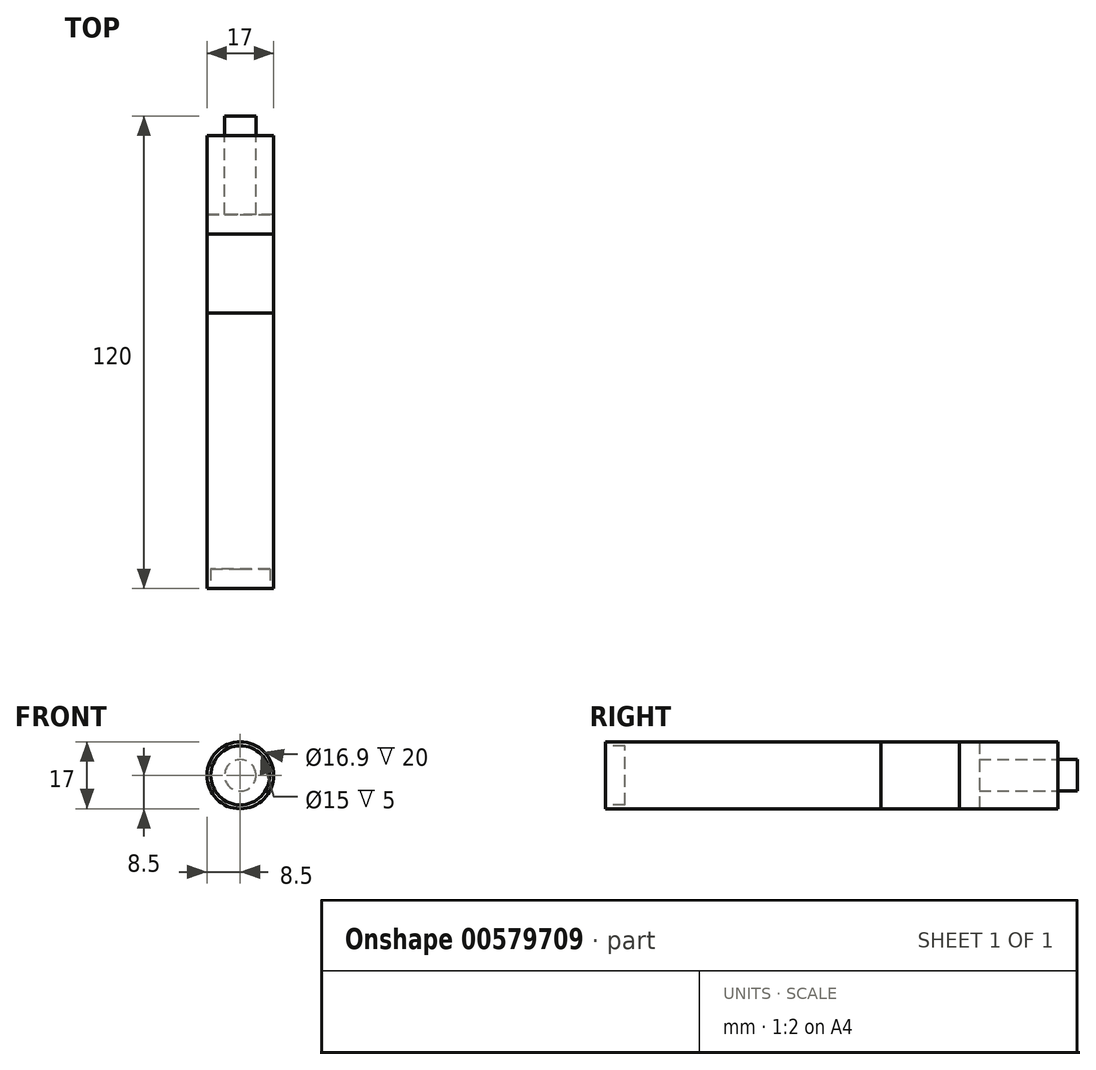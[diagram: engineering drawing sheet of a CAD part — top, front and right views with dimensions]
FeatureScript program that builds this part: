
annotation { "Feature Type Name" : "Feature", "Feature Type Description" : "" }
export const myFeature = defineFeature(function(context is Context, id is Id, definition is map)
    precondition{}
    {
        {
            var Q0;
            Q0=qCreatedBy(makeId("Front.planeOp"),FACE);
            var sketch = newSketch(context, id + "F0", { "sketchPlane" : qUnion([Q0])});
            skCircle(sketch, "E0", {"center": v(0, 0) * mm, "radius": 8.5 * mm});
            skSolve(sketch);
        }
        {
            var Q0;
            Q0=makeQuery(id+"F0.imprint","IMPRINT",FACE,{"disambiguationData":[TD([[makeQuery(id+"F0.imprint","IMPRINT",EDGE,{"derivedFrom":sQuery(id+"F0.wireOp",EDGE,"E0")}),1.0]])]});
            extrude(context, id + "F1", {"entities" : qUnion([Q0]), "depth" : 90 * mm, "offsetDistance" : 25 * mm});
        }
        {
            var Q0;
            Q0=qCreatedBy(makeId("Front.planeOp"),FACE);
            var sketch = newSketch(context, id + "F2", { "sketchPlane" : qUnion([Q0])});
            skCircle(sketch, "E1", {"center": v(0, 0) * mm, "radius": 8.5 * mm});
            skSolve(sketch);
        }
        {
            var Q0;
            Q0 = qSketchRegion(id + "F2", true);
            extrude(context, id + "F3", {"entities" : qUnion([Q0]), "depth" : 20 * mm, "offsetDistance" : 25 * mm, "hasSecondDirection" : true, "secondDirectionOppositeDirection" : true, "secondDirectionDepth" : 25 * mm});
        }
        {
            var Q0;
            Q0=makeQuery(id+"F3.opExtrude","CAP_FACE",FACE,{"disambiguationData":[OSD([sQuery(id+"F2.wireOp",EDGE,"E1")])],"isStart":true});
            var sketch = newSketch(context, id + "F4", { "sketchPlane" : qUnion([Q0])});
            skCircle(sketch, "E2", {"center": v(0, 0) * mm, "radius": 4 * mm});
            skSolve(sketch);
        }
        {
            var Q0;
            Q0 = qSketchRegion(id + "F4", true);
            extrude(context, id + "F5", {"entities" : qUnion([Q0]), "depth" : 5 * mm, "offsetDistance" : 25 * mm});
        }
        {
            var Q0;
            Q0=makeQuery(id+"F3.opExtrude","CAP_FACE",FACE,{"disambiguationData":[OSD([sQuery(id+"F2.wireOp",EDGE,"E1")])],"isStart":true});
            var sketch = newSketch(context, id + "F6", { "sketchPlane" : qUnion([Q0])});
            skCircle(sketch, "E3", {"center": v(0, 0) * mm, "radius": 8.45 * mm});
            skSolve(sketch);
        }
        {
            var Q0;
            Q0=makeQuery(id+"F6.imprint","IMPRINT",FACE,{"disambiguationData":[TD([[makeQuery(id+"F6.imprint","IMPRINT",EDGE,{"derivedFrom":sQuery(id+"F6.wireOp",EDGE,"E3")}),1.0]])]});
            extrude(context, id + "F7", {"entities" : qUnion([Q0]), "operationType" : NewBodyOperationType.REMOVE, "oppositeDirection" : true, "depth" : 20 * mm, "offsetDistance" : 25 * mm});
        }
        {
            var Q0;
            Q0 = qSketchRegion(id + "F4", true);
            extrude(context, id + "F8", {"entities" : qUnion([Q0]), "oppositeDirection" : true, "depth" : 20 * mm, "offsetDistance" : 25 * mm});
        }
        {
            var Q0;
            Q0=makeQuery(id+"F1.opExtrude","CAP_FACE",FACE,{"disambiguationData":[OSD([sQuery(id+"F0.wireOp",EDGE,"E0")])],"isStart":false});
            var sketch = newSketch(context, id + "F9", { "sketchPlane" : qUnion([Q0])});
            skCircle(sketch, "E4", {"center": v(0, 0) * mm, "radius": 8.5 * mm});
            skSolve(sketch);
        }
        {
            var Q0;
            Q0=makeQuery(id+"F9.imprint","IMPRINT",FACE,{"disambiguationData":[TD([[makeQuery(id+"F9.imprint","IMPRINT",EDGE,{"derivedFrom":sQuery(id+"F9.wireOp",EDGE,"E4")}),1.0]])]});
            var sketch = newSketch(context, id + "F10", { "sketchPlane" : qUnion([Q0])});
            skCircle(sketch, "E5", {"center": v(0, 0) * mm, "radius": 7.5 * mm});
            skSolve(sketch);
        }
        {
            var Q0;
            Q0 = qSketchRegion(id + "F10", true);
            extrude(context, id + "F11", {"entities" : qUnion([Q0]), "operationType" : NewBodyOperationType.REMOVE, "oppositeDirection" : true, "depth" : 5 * mm, "offsetDistance" : 25 * mm});
        }
        {
            var Q0;
            Q0=makeQuery(id+"F9.imprint","IMPRINT",FACE,{"disambiguationData":[TD([[makeQuery(id+"F9.imprint","IMPRINT",EDGE,{"derivedFrom":sQuery(id+"F9.wireOp",EDGE,"E4")}),1.0]])]});
            var sketch = newSketch(context, id + "F12", { "sketchPlane" : qUnion([Q0])});
            skLineSegment(sketch, "E6", {"start": v(0, -7.42) * mm, "end": v(0, -4.42) * mm});
            skLineSegment(sketch, "E7", {"start": v(0, 7.48) * mm, "end": v(0, 4.48) * mm});
            skLineSegment(sketch, "E8", {"start": v(-7.53, 0) * mm, "end": v(-4.53, 0) * mm});
            skLineSegment(sketch, "E9", {"start": v(7.45, 0) * mm, "end": v(4.45, 0) * mm});
            skSolve(sketch);
        }
        {
            var Q0;
            Q0=sQuery(id+"F12.wireOp",EDGE,"E7");
            extrude(context, id + "F13", {"bodyType" : ToolBodyType.SURFACE, "surfaceEntities" : qUnion([Q0]), "oppositeDirection" : true, "depth" : 5 * mm, "offsetDistance" : 25 * mm});
        }
        {
            var Q0;
            Q0=sQuery(id+"F12.wireOp",EDGE,"E8");
            extrude(context, id + "F14", {"bodyType" : ToolBodyType.SURFACE, "surfaceEntities" : qUnion([Q0]), "oppositeDirection" : true, "depth" : 5 * mm, "offsetDistance" : 25 * mm});
        }
        {
            var Q0;
            Q0=sQuery(id+"F12.wireOp",EDGE,"E9");
            extrude(context, id + "F15", {"bodyType" : ToolBodyType.SURFACE, "surfaceEntities" : qUnion([Q0]), "oppositeDirection" : true, "depth" : 5 * mm, "offsetDistance" : 25 * mm});
        }
        {
            var Q0;
            Q0=sQuery(id+"F12.wireOp",EDGE,"E6");
            extrude(context, id + "F16", {"bodyType" : ToolBodyType.SURFACE, "surfaceEntities" : qUnion([Q0]), "oppositeDirection" : true, "depth" : 5 * mm, "offsetDistance" : 25 * mm});
        }
        {
            var Q0;
            Q0=makeQuery(id+"F10.imprint","IMPRINT",FACE,{"disambiguationData":[TD([[makeQuery(id+"F10.imprint","IMPRINT",EDGE,{"derivedFrom":sQuery(id+"F10.wireOp",EDGE,"E5")}),1.0]])]});
            var sketch = newSketch(context, id + "F17", { "sketchPlane" : qUnion([Q0])});
            skLineSegment(sketch, "E10", {"start": v(0, 0) * mm, "end": v(0, 0) * mm});
            skLineSegment(sketch, "E11", {"start": v(3.1, -3.1) * mm, "end": v(5.22, -5.22) * mm});
            skLineSegment(sketch, "E12", {"start": v(5.22, -5.22) * mm, "end": v(3.1, -3.1) * mm});
            skLineSegment(sketch, "E13", {"start": v(-3.14, 3.14) * mm, "end": v(-5.27, 5.27) * mm});
            skLineSegment(sketch, "E14", {"start": v(-5.27, 5.27) * mm, "end": v(-3.14, 3.14) * mm});
            skLineSegment(sketch, "E15", {"start": v(3.14, 3.14) * mm, "end": v(5.27, 5.27) * mm});
            skLineSegment(sketch, "E16", {"start": v(5.27, 5.27) * mm, "end": v(3.14, 3.14) * mm});
            skLineSegment(sketch, "E17", {"start": v(-3.14, -3.14) * mm, "end": v(-5.27, -5.27) * mm});
            skLineSegment(sketch, "E18", {"start": v(-5.27, -5.27) * mm, "end": v(-3.14, -3.14) * mm});
            skPoint(sketch, "E19.start.orphan", {"position": v(0, -7.41) * mm});
            skSolve(sketch);
        }
        {
            var Q0;
            Q0=sQuery(id+"F17.wireOp",EDGE,"E14");
            extrude(context, id + "F18", {"bodyType" : ToolBodyType.SURFACE, "surfaceEntities" : qUnion([Q0]), "oppositeDirection" : true, "depth" : 5 * mm, "offsetDistance" : 25 * mm});
        }
        {
            var Q0;
            Q0=sQuery(id+"F17.wireOp",EDGE,"E16");
            extrude(context, id + "F19", {"bodyType" : ToolBodyType.SURFACE, "surfaceEntities" : qUnion([Q0]), "oppositeDirection" : true, "depth" : 5 * mm, "offsetDistance" : 25 * mm});
        }
        {
            var Q0;
            Q0=sQuery(id+"F17.wireOp",EDGE,"E18");
            extrude(context, id + "F20", {"bodyType" : ToolBodyType.SURFACE, "surfaceEntities" : qUnion([Q0]), "oppositeDirection" : true, "depth" : 5 * mm, "offsetDistance" : 25 * mm});
        }
        {
            var Q0;
            Q0=sQuery(id+"F17.wireOp",EDGE,"E12");
            extrude(context, id + "F21", {"bodyType" : ToolBodyType.SURFACE, "surfaceEntities" : qUnion([Q0]), "oppositeDirection" : true, "depth" : 5 * mm, "offsetDistance" : 25 * mm});
        }
    });
